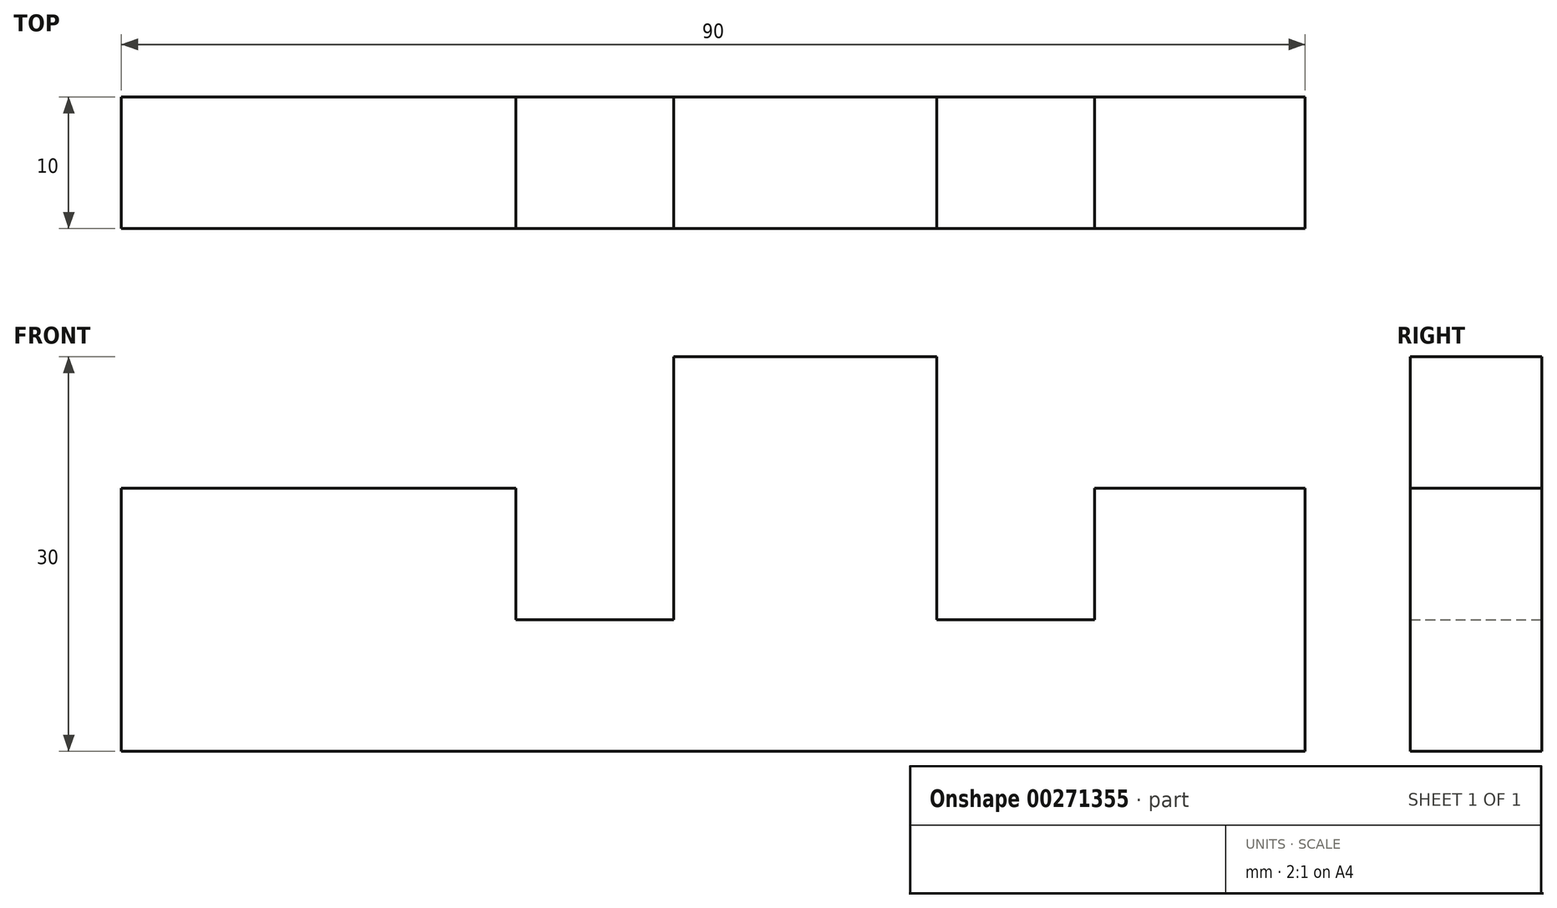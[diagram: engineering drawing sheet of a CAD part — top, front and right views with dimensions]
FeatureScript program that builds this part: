
annotation { "Feature Type Name" : "Feature", "Feature Type Description" : "" }
export const myFeature = defineFeature(function(context is Context, id is Id, definition is map)
    precondition{}
    {
        {
            var Q0;
            Q0=qCreatedBy(makeId("Front.planeOp"),FACE);
            var sketch = newSketch(context, id + "F0", { "sketchPlane" : qUnion([Q0])});
            skLineSegment(sketch, "E0", {"start": v(0, 0) * mm, "end": v(90, 0) * mm});
            skLineSegment(sketch, "E1", {"start": v(0, 0) * mm, "end": v(0, 20) * mm});
            skLineSegment(sketch, "E2", {"start": v(0, 20) * mm, "end": v(30, 20) * mm});
            skLineSegment(sketch, "E3", {"start": v(30, 20) * mm, "end": v(30, 10) * mm});
            skLineSegment(sketch, "E4", {"start": v(30, 10) * mm, "end": v(42, 10) * mm});
            skLineSegment(sketch, "E5", {"start": v(42, 20) * mm, "end": v(42, 10) * mm});
            skLineSegment(sketch, "E6", {"start": v(42, 20) * mm, "end": v(42, 30) * mm});
            skLineSegment(sketch, "E7", {"start": v(42, 30) * mm, "end": v(62, 30) * mm});
            skLineSegment(sketch, "E8", {"start": v(62, 30) * mm, "end": v(62, 10) * mm});
            skLineSegment(sketch, "E9", {"start": v(62, 10) * mm, "end": v(74, 10) * mm});
            skLineSegment(sketch, "E10", {"start": v(74, 10) * mm, "end": v(74, 20) * mm});
            skLineSegment(sketch, "E11", {"start": v(74, 20) * mm, "end": v(90, 20) * mm});
            skLineSegment(sketch, "E12", {"start": v(90, 20) * mm, "end": v(90, 0) * mm});
            skSolve(sketch);
        }
        {
            var Q0;
            Q0=makeQuery(id+"F0.imprint","IMPRINT",FACE,{"disambiguationData":[TD([[makeQuery(id+"F0.imprint","IMPRINT",EDGE,{"derivedFrom":sQuery(id+"F0.wireOp",EDGE,"E0")}),1.0]])]});
            extrude(context, id + "F1", {"entities" : qUnion([Q0]), "depth" : 10 * mm});
        }
    });
